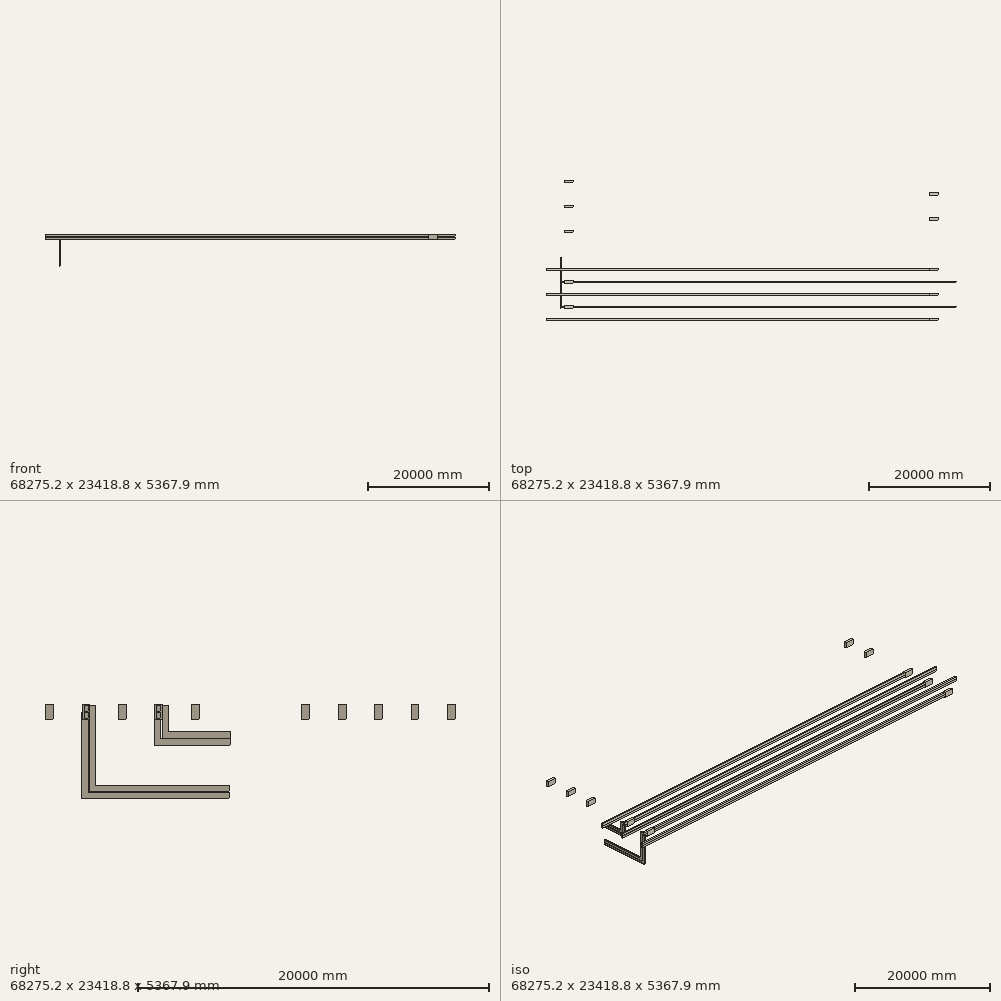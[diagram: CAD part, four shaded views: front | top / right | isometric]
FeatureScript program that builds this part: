
annotation { "Feature Type Name" : "Feature", "Feature Type Description" : "" }
export const myFeature = defineFeature(function(context is Context, id is Id, definition is map)
    precondition{}
    {
        {
            var Q0;
            Q0=qCreatedBy(makeId("Top.planeOp"),FACE);
            var sketch = newSketch(context, id + "F0", { "sketchPlane" : qUnion([Q0])});
            skLineSegment(sketch, "E0.bottom", {"start": v(-34137.6, 13411.2) * mm, "end": v(34137.6, 13411.2) * mm});
            skLineSegment(sketch, "E0.top", {"start": v(-34137.6, -13411.2) * mm, "end": v(34137.6, -13411.2) * mm});
            skLineSegment(sketch, "E0.left", {"start": v(-34137.6, 13411.2) * mm, "end": v(-34137.6, -13411.2) * mm});
            skLineSegment(sketch, "E0.right", {"start": v(34137.6, 13411.2) * mm, "end": v(34137.6, -13411.2) * mm});
            skPoint(sketch, "E0.middle", {"position": v(0, 0) * mm});
            skLineSegment(sketch, "E1", {"start": v(-31699.2, 13411.2) * mm, "end": v(-31699.2, 1219.2) * mm});
            skLineSegment(sketch, "E2", {"start": v(31699.2, 13411.2) * mm, "end": v(31699.2, 1219.2) * mm});
            skLineSegment(sketch, "E3", {"start": v(-31699.2, 1219.2) * mm, "end": v(-2438.4, 1219.2) * mm});
            skLineSegment(sketch, "E4", {"start": v(-31699.2, -1219.2) * mm, "end": v(-2438.4, -1219.2) * mm});
            skLineSegment(sketch, "E5", {"start": v(-2438.4, 13411.2) * mm, "end": v(-2438.4, 1219.2) * mm});
            skLineSegment(sketch, "E6", {"start": v(2438.4, 13411.2) * mm, "end": v(2438.4, 1219.2) * mm});
            skLineSegment(sketch, "E7.trimOffspring", {"start": v(-2438.4, -1219.2) * mm, "end": v(-2438.4, -13411.2) * mm});
            skLineSegment(sketch, "E8.trimOffspring", {"start": v(2438.4, 1219.2) * mm, "end": v(31699.2, 1219.2) * mm});
            skLineSegment(sketch, "E9.trimOffspring", {"start": v(2438.4, -1219.2) * mm, "end": v(31699.2, -1219.2) * mm});
            skLineSegment(sketch, "E10.trimOffspring", {"start": v(2438.4, -1219.2) * mm, "end": v(2438.4, -13411.2) * mm});
            skLineSegment(sketch, "E11.trimOffspring", {"start": v(-31699.2, -1219.2) * mm, "end": v(-31699.2, -13411.2) * mm});
            skLineSegment(sketch, "E12.trimOffspring", {"start": v(31699.2, -1219.2) * mm, "end": v(31699.2, -13411.2) * mm});
            skSolve(sketch);
        }
        {
            var Q0;
            {var subQ0=sQuery(id+"F0.wireOp",EDGE,"E1");Q0=makeQuery(id+"F0.imprint","IMPRINT",FACE,{"disambiguationData":[TD([[makeQuery(id+"F0.imprint","IMPRINT",EDGE,{"derivedFrom":subQ0}),1.0]])]});}
            var sketch = newSketch(context, id + "F1", { "sketchPlane" : qUnion([Q0])});
            skLineSegment(sketch, "E13.bottom", {"start": v(-31089.6, 2921) * mm, "end": v(-29616.4, 2921) * mm});
            skLineSegment(sketch, "E13.top", {"start": v(-31089.6, 3352.8) * mm, "end": v(-29616.4, 3352.8) * mm});
            skLineSegment(sketch, "E13.left", {"start": v(-31089.6, 2921) * mm, "end": v(-31089.6, 3352.8) * mm});
            skLineSegment(sketch, "E13.right", {"start": v(-29616.4, 2921) * mm, "end": v(-29616.4, 3352.8) * mm});
            skLineSegment(sketch, "E14.bottom", {"start": v(-31089.6, 7099.3) * mm, "end": v(-29616.4, 7099.3) * mm});
            skLineSegment(sketch, "E14.top", {"start": v(-31089.6, 7531.1) * mm, "end": v(-29616.4, 7531.1) * mm});
            skLineSegment(sketch, "E14.left", {"start": v(-31089.6, 7099.3) * mm, "end": v(-31089.6, 7531.1) * mm});
            skLineSegment(sketch, "E14.right", {"start": v(-29616.4, 7099.3) * mm, "end": v(-29616.4, 7531.1) * mm});
            skLineSegment(sketch, "E15.bottom", {"start": v(-31089.6, 11277.6) * mm, "end": v(-29616.4, 11277.6) * mm});
            skLineSegment(sketch, "E15.top", {"start": v(-31089.6, 11709.4) * mm, "end": v(-29616.4, 11709.4) * mm});
            skLineSegment(sketch, "E15.left", {"start": v(-31089.6, 11277.6) * mm, "end": v(-31089.6, 11709.4) * mm});
            skLineSegment(sketch, "E15.right", {"start": v(-29616.4, 11277.6) * mm, "end": v(-29616.4, 11709.4) * mm});
            skLineSegment(sketch, "E16.bottom", {"start": v(-31089.6, -9169.4) * mm, "end": v(-29616.4, -9169.4) * mm});
            skLineSegment(sketch, "E16.top", {"start": v(-31089.6, -9601.2) * mm, "end": v(-29616.4, -9601.2) * mm});
            skLineSegment(sketch, "E16.left", {"start": v(-31089.6, -9169.4) * mm, "end": v(-31089.6, -9601.2) * mm});
            skLineSegment(sketch, "E16.right", {"start": v(-29616.4, -9169.4) * mm, "end": v(-29616.4, -9601.2) * mm});
            skPoint(sketch, "E17.left.start.orphan", {"position": v(-31089.6, -5029.2) * mm});
            skLineSegment(sketch, "E18.bottom", {"start": v(-31089.6, -5029.2) * mm, "end": v(-29616.4, -5029.2) * mm});
            skLineSegment(sketch, "E18.top", {"start": v(-31089.6, -5461) * mm, "end": v(-29616.4, -5461) * mm});
            skLineSegment(sketch, "E18.left", {"start": v(-31089.6, -5029.2) * mm, "end": v(-31089.6, -5461) * mm});
            skLineSegment(sketch, "E18.right", {"start": v(-29616.4, -5029.2) * mm, "end": v(-29616.4, -5461) * mm});
            skLineSegment(sketch, "E19.bottom", {"start": v(31089.6, -7531.1) * mm, "end": v(29616.4, -7531.1) * mm});
            skLineSegment(sketch, "E19.top", {"start": v(31089.6, -7099.3) * mm, "end": v(29616.4, -7099.3) * mm});
            skLineSegment(sketch, "E19.left", {"start": v(31089.6, -7531.1) * mm, "end": v(31089.6, -7099.3) * mm});
            skLineSegment(sketch, "E19.right", {"start": v(29616.4, -7531.1) * mm, "end": v(29616.4, -7099.3) * mm});
            skLineSegment(sketch, "E20.bottom", {"start": v(31089.6, -11709.4) * mm, "end": v(29616.4, -11709.4) * mm});
            skLineSegment(sketch, "E20.top", {"start": v(31089.6, -11277.6) * mm, "end": v(29616.4, -11277.6) * mm});
            skLineSegment(sketch, "E20.left", {"start": v(31089.6, -11709.4) * mm, "end": v(31089.6, -11277.6) * mm});
            skLineSegment(sketch, "E20.right", {"start": v(29616.4, -11709.4) * mm, "end": v(29616.4, -11277.6) * mm});
            skLineSegment(sketch, "E21.bottom", {"start": v(31089.6, -3352.8) * mm, "end": v(29616.4, -3352.8) * mm});
            skLineSegment(sketch, "E21.top", {"start": v(31089.6, -2921) * mm, "end": v(29616.4, -2921) * mm});
            skLineSegment(sketch, "E21.left", {"start": v(31089.6, -3352.8) * mm, "end": v(31089.6, -2921) * mm});
            skLineSegment(sketch, "E21.right", {"start": v(29616.4, -3352.8) * mm, "end": v(29616.4, -2921) * mm});
            skPoint(sketch, "E22.oppositeSnap0", {"position": v(29616.4, -3136.9) * mm});
            skLineSegment(sketch, "E22.bottom", {"start": v(31089.6, 5029.2) * mm, "end": v(29616.4, 5029.2) * mm});
            skLineSegment(sketch, "E22.top", {"start": v(31089.6, 5461) * mm, "end": v(29616.4, 5461) * mm});
            skLineSegment(sketch, "E22.left", {"start": v(31089.6, 5029.2) * mm, "end": v(31089.6, 5461) * mm});
            skLineSegment(sketch, "E22.right", {"start": v(29616.4, 5029.2) * mm, "end": v(29616.4, 5461) * mm});
            skLineSegment(sketch, "E23.bottom", {"start": v(31089.6, 9169.4) * mm, "end": v(29616.4, 9169.4) * mm});
            skLineSegment(sketch, "E23.top", {"start": v(31089.6, 9601.2) * mm, "end": v(29616.4, 9601.2) * mm});
            skLineSegment(sketch, "E23.left", {"start": v(31089.6, 9169.4) * mm, "end": v(31089.6, 9601.2) * mm});
            skLineSegment(sketch, "E23.right", {"start": v(29616.4, 9169.4) * mm, "end": v(29616.4, 9601.2) * mm});
            skSolve(sketch);
        }
        {
            var Q0;
            Q0=qSketchRegion(id+"F1",true);
            extrude(context, id + "F2", {"entities" : qUnion([Q0]), "depth" : 838.2 * mm, "offsetDistance" : 25.4 * mm});
        }
        {
            var Q0;
            Q0=makeQuery(id+"F2.opExtrude","SWEPT_FACE",FACE,{"disambiguationData":[OSD([sQuery(id+"F1.wireOp",EDGE,"E16.right")])]});
            var sketch = newSketch(context, id + "F3", { "sketchPlane" : qUnion([Q0])});
            skLineSegment(sketch, "E24.bottom", {"start": v(-9271, 42.33) * mm, "end": v(-9499.6, 42.33) * mm});
            skLineSegment(sketch, "E24.top", {"start": v(-9271, 397.93) * mm, "end": v(-9499.6, 397.93) * mm});
            skLineSegment(sketch, "E24.left", {"start": v(-9271, 42.33) * mm, "end": v(-9271, 397.93) * mm});
            skLineSegment(sketch, "E24.right", {"start": v(-9499.6, 42.33) * mm, "end": v(-9499.6, 397.93) * mm});
            skPoint(sketch, "E24.middle", {"position": v(-9385.3, 220.13) * mm});
            skPoint(sketch, "E24.middle.positionSnap0", {"position": v(-9385.3, 0) * mm});
            skPoint(sketch, "E24.centerSnap0", {"position": v(-9385.3, 0) * mm});
            skLineSegment(sketch, "E25.bottom", {"start": v(-9499.6, 440.27) * mm, "end": v(-9271, 440.27) * mm});
            skLineSegment(sketch, "E25.top", {"start": v(-9499.6, 795.87) * mm, "end": v(-9271, 795.87) * mm});
            skLineSegment(sketch, "E25.left", {"start": v(-9499.6, 440.27) * mm, "end": v(-9499.6, 795.87) * mm});
            skLineSegment(sketch, "E25.right", {"start": v(-9271, 440.27) * mm, "end": v(-9271, 795.87) * mm});
            skPoint(sketch, "E25.middle", {"position": v(-9385.3, 618.07) * mm});
            skLineSegment(sketch, "E26.bottom", {"start": v(-5359.4, 397.93) * mm, "end": v(-5130.8, 397.93) * mm});
            skLineSegment(sketch, "E26.top", {"start": v(-5359.4, 42.33) * mm, "end": v(-5130.8, 42.33) * mm});
            skLineSegment(sketch, "E26.left", {"start": v(-5359.4, 397.93) * mm, "end": v(-5359.4, 42.33) * mm});
            skLineSegment(sketch, "E26.right", {"start": v(-5130.8, 397.93) * mm, "end": v(-5130.8, 42.33) * mm});
            skPoint(sketch, "E26.middle", {"position": v(-5245.1, 220.13) * mm});
            skLineSegment(sketch, "E27.bottom", {"start": v(-5359.4, 440.27) * mm, "end": v(-5130.8, 440.27) * mm});
            skLineSegment(sketch, "E27.top", {"start": v(-5359.4, 795.87) * mm, "end": v(-5130.8, 795.87) * mm});
            skLineSegment(sketch, "E27.left", {"start": v(-5359.4, 440.27) * mm, "end": v(-5359.4, 795.87) * mm});
            skLineSegment(sketch, "E27.right", {"start": v(-5130.8, 440.27) * mm, "end": v(-5130.8, 795.87) * mm});
            skPoint(sketch, "E27.middle", {"position": v(-5245.1, 618.07) * mm});
            skSolve(sketch);
        }
        {
            var Q0;
            Q0=qSketchRegion(id+"F3",true);
            extrude(context, id + "F4", {"entities" : qUnion([Q0]), "depth" : 63754 * mm, "offsetDistance" : 25.4 * mm});
        }
        {
            var Q0;
            Q0=makeQuery(id+"F2.opExtrude","SWEPT_FACE",FACE,{"disambiguationData":[OSD([sQuery(id+"F1.wireOp",EDGE,"E21.right")])]});
            var sketch = newSketch(context, id + "F5", { "sketchPlane" : qUnion([Q0])});
            skLineSegment(sketch, "E28.bottom", {"start": v(3022.6, 397.93) * mm, "end": v(3251.2, 397.93) * mm});
            skLineSegment(sketch, "E28.top", {"start": v(3022.6, 42.33) * mm, "end": v(3251.2, 42.33) * mm});
            skLineSegment(sketch, "E28.left", {"start": v(3022.6, 397.93) * mm, "end": v(3022.6, 42.33) * mm});
            skLineSegment(sketch, "E28.right", {"start": v(3251.2, 397.93) * mm, "end": v(3251.2, 42.33) * mm});
            skPoint(sketch, "E28.middle", {"position": v(3136.9, 220.13) * mm});
            skPoint(sketch, "E28.middle.positionSnap0", {"position": v(3136.9, 0) * mm});
            skPoint(sketch, "E28.centerSnap0", {"position": v(3136.9, 0) * mm});
            skLineSegment(sketch, "E29.bottom", {"start": v(3022.6, 440.27) * mm, "end": v(3251.2, 440.27) * mm});
            skLineSegment(sketch, "E29.top", {"start": v(3022.6, 795.87) * mm, "end": v(3251.2, 795.87) * mm});
            skLineSegment(sketch, "E29.left", {"start": v(3022.6, 440.27) * mm, "end": v(3022.6, 795.87) * mm});
            skLineSegment(sketch, "E29.right", {"start": v(3251.2, 440.27) * mm, "end": v(3251.2, 795.87) * mm});
            skPoint(sketch, "E29.middle", {"position": v(3136.9, 618.07) * mm});
            skLineSegment(sketch, "E30.bottom", {"start": v(7200.9, 397.93) * mm, "end": v(7429.5, 397.93) * mm});
            skLineSegment(sketch, "E30.top", {"start": v(7200.9, 42.33) * mm, "end": v(7429.5, 42.33) * mm});
            skLineSegment(sketch, "E30.left", {"start": v(7200.9, 397.93) * mm, "end": v(7200.9, 42.33) * mm});
            skLineSegment(sketch, "E30.right", {"start": v(7429.5, 397.93) * mm, "end": v(7429.5, 42.33) * mm});
            skPoint(sketch, "E30.middle", {"position": v(7315.2, 220.13) * mm});
            skLineSegment(sketch, "E31.bottom", {"start": v(7200.9, 795.87) * mm, "end": v(7429.5, 795.87) * mm});
            skLineSegment(sketch, "E31.top", {"start": v(7200.9, 440.27) * mm, "end": v(7429.5, 440.27) * mm});
            skLineSegment(sketch, "E31.left", {"start": v(7200.9, 795.87) * mm, "end": v(7200.9, 440.27) * mm});
            skLineSegment(sketch, "E31.right", {"start": v(7429.5, 795.87) * mm, "end": v(7429.5, 440.27) * mm});
            skPoint(sketch, "E31.middle", {"position": v(7315.2, 618.07) * mm});
            skLineSegment(sketch, "E32.bottom", {"start": v(11379.2, 397.93) * mm, "end": v(11607.8, 397.93) * mm});
            skLineSegment(sketch, "E32.top", {"start": v(11379.2, 42.33) * mm, "end": v(11607.8, 42.33) * mm});
            skLineSegment(sketch, "E32.left", {"start": v(11379.2, 397.93) * mm, "end": v(11379.2, 42.33) * mm});
            skLineSegment(sketch, "E32.right", {"start": v(11607.8, 397.93) * mm, "end": v(11607.8, 42.33) * mm});
            skPoint(sketch, "E32.middle", {"position": v(11493.5, 220.13) * mm});
            skLineSegment(sketch, "E33.bottom", {"start": v(11379.2, 440.27) * mm, "end": v(11607.8, 440.27) * mm});
            skLineSegment(sketch, "E33.top", {"start": v(11379.2, 795.87) * mm, "end": v(11607.8, 795.87) * mm});
            skLineSegment(sketch, "E33.left", {"start": v(11379.2, 440.27) * mm, "end": v(11379.2, 795.87) * mm});
            skLineSegment(sketch, "E33.right", {"start": v(11607.8, 440.27) * mm, "end": v(11607.8, 795.87) * mm});
            skPoint(sketch, "E33.middle", {"position": v(11493.5, 618.07) * mm});
            skSolve(sketch);
        }
        {
            var Q0;
            Q0=qSketchRegion(id+"F5",true);
            extrude(context, id + "F6", {"entities" : qUnion([Q0]), "depth" : 63754 * mm, "offsetDistance" : 25.4 * mm});
        }
        {
            var Q0;
            Q0=makeQuery(id+"F2.opExtrude","SWEPT_FACE",FACE,{"disambiguationData":[OSD([sQuery(id+"F1.wireOp",EDGE,"E18.left")])]});
            var sketch = newSketch(context, id + "F7", { "sketchPlane" : qUnion([Q0])});
            skLineSegment(sketch, "E34.bottom", {"start": v(5130.8, 397.93) * mm, "end": v(5359.4, 397.93) * mm});
            skLineSegment(sketch, "E34.top", {"start": v(5130.8, 42.33) * mm, "end": v(5359.4, 42.33) * mm});
            skLineSegment(sketch, "E34.left", {"start": v(5130.8, 397.93) * mm, "end": v(5130.8, 42.33) * mm});
            skLineSegment(sketch, "E34.right", {"start": v(5359.4, 397.93) * mm, "end": v(5359.4, 42.33) * mm});
            skPoint(sketch, "E34.middle", {"position": v(5245.1, 220.13) * mm});
            skPoint(sketch, "E34.middle.positionSnap0", {"position": v(5245.1, 0) * mm});
            skPoint(sketch, "E34.centerSnap0", {"position": v(5245.1, 0) * mm});
            skLineSegment(sketch, "E35.bottom", {"start": v(5130.8, 440.27) * mm, "end": v(5359.4, 440.27) * mm});
            skLineSegment(sketch, "E35.top", {"start": v(5130.8, 795.87) * mm, "end": v(5359.4, 795.87) * mm});
            skLineSegment(sketch, "E35.left", {"start": v(5130.8, 440.27) * mm, "end": v(5130.8, 795.87) * mm});
            skLineSegment(sketch, "E35.right", {"start": v(5359.4, 440.27) * mm, "end": v(5359.4, 795.87) * mm});
            skPoint(sketch, "E35.middle", {"position": v(5245.1, 618.07) * mm});
            skLineSegment(sketch, "E36.bottom", {"start": v(9271, 42.33) * mm, "end": v(9499.6, 42.33) * mm});
            skLineSegment(sketch, "E36.top", {"start": v(9271, 397.93) * mm, "end": v(9499.6, 397.93) * mm});
            skLineSegment(sketch, "E36.left", {"start": v(9271, 42.33) * mm, "end": v(9271, 397.93) * mm});
            skLineSegment(sketch, "E36.right", {"start": v(9499.6, 42.33) * mm, "end": v(9499.6, 397.93) * mm});
            skPoint(sketch, "E36.middle", {"position": v(9385.3, 220.13) * mm});
            skLineSegment(sketch, "E37.bottom", {"start": v(9271, 440.27) * mm, "end": v(9499.6, 440.27) * mm});
            skLineSegment(sketch, "E37.top", {"start": v(9271, 795.87) * mm, "end": v(9499.6, 795.87) * mm});
            skLineSegment(sketch, "E37.left", {"start": v(9271, 440.27) * mm, "end": v(9271, 795.87) * mm});
            skLineSegment(sketch, "E37.right", {"start": v(9499.6, 440.27) * mm, "end": v(9499.6, 795.87) * mm});
            skPoint(sketch, "E37.middle", {"position": v(9385.3, 618.07) * mm});
            skSolve(sketch);
        }
        {
            var Q0;
            Q0 = qSketchRegion(id + "F7", true);
            extrude(context, id + "F8", {"entities" : qUnion([Q0]), "depth" : 723.9 * mm, "offsetDistance" : 25.4 * mm});
        }
        {
            var Q0;
            Q0=makeQuery(id+"F8.opExtrude","SWEPT_FACE",FACE,{"disambiguationData":[OSD([sQuery(id+"F7.wireOp",EDGE,"E35.left")])]});
            var sketch = newSketch(context, id + "F9", { "sketchPlane" : qUnion([Q0])});
            skLineSegment(sketch, "E38.bottom", {"start": v(31813.5, 795.87) * mm, "end": v(31584.9, 795.87) * mm});
            skLineSegment(sketch, "E38.top", {"start": v(31813.5, 440.27) * mm, "end": v(31584.9, 440.27) * mm});
            skLineSegment(sketch, "E38.left", {"start": v(31813.5, 795.87) * mm, "end": v(31813.5, 440.27) * mm});
            skLineSegment(sketch, "E38.right", {"start": v(31584.9, 795.87) * mm, "end": v(31584.9, 440.27) * mm});
            skSolve(sketch);
        }
        {
            var Q0;
            Q0 = qSketchRegion(id + "F9", true);
            extrude(context, id + "F10", {"entities" : qUnion([Q0]), "operationType" : NewBodyOperationType.ADD, "depth" : 431.8 * mm, "offsetDistance" : 25.4 * mm});
        }
        {
            var Q0;
            Q0=makeQuery(id+"F8.opExtrude","SWEPT_FACE",FACE,{"disambiguationData":[OSD([sQuery(id+"F7.wireOp",EDGE,"E34.right")])]});
            var sketch = newSketch(context, id + "F11", { "sketchPlane" : qUnion([Q0])});
            skLineSegment(sketch, "E39.bottom", {"start": v(-31813.5, 42.33) * mm, "end": v(-31584.9, 42.33) * mm});
            skLineSegment(sketch, "E39.top", {"start": v(-31813.5, 397.93) * mm, "end": v(-31584.9, 397.93) * mm});
            skLineSegment(sketch, "E39.left", {"start": v(-31813.5, 42.33) * mm, "end": v(-31813.5, 397.93) * mm});
            skLineSegment(sketch, "E39.right", {"start": v(-31584.9, 42.33) * mm, "end": v(-31584.9, 397.93) * mm});
            skSolve(sketch);
        }
        {
            var Q0;
            Q0 = qSketchRegion(id + "F11", true);
            extrude(context, id + "F12", {"entities" : qUnion([Q0]), "operationType" : NewBodyOperationType.ADD, "depth" : 127 * mm, "offsetDistance" : 25.4 * mm});
        }
        {
            var Q0;
            Q0=makeQuery(id+"F12.boolean.opBoolean","MERGE",FACE,{"derivedFrom":[makeQuery(id+"F8.opExtrude","SWEPT_FACE",FACE,{"disambiguationData":[OSD([sQuery(id+"F7.wireOp",EDGE,"E34.top")])]}),makeQuery(id+"F12.opExtrude","SWEPT_FACE",FACE,{"disambiguationData":[OSD([sQuery(id+"F11.wireOp",EDGE,"E39.bottom")])]})]});
            var sketch = newSketch(context, id + "F13", { "sketchPlane" : qUnion([Q0])});
            skLineSegment(sketch, "E40.bottom", {"start": v(-31813.5, 5486.4) * mm, "end": v(-31584.9, 5486.4) * mm});
            skLineSegment(sketch, "E40.top", {"start": v(-31813.5, 5130.8) * mm, "end": v(-31584.9, 5130.8) * mm});
            skLineSegment(sketch, "E40.left", {"start": v(-31813.5, 5486.4) * mm, "end": v(-31813.5, 5130.8) * mm});
            skLineSegment(sketch, "E40.right", {"start": v(-31584.9, 5486.4) * mm, "end": v(-31584.9, 5130.8) * mm});
            skSolve(sketch);
        }
        {
            var Q0;
            Q0 = qSketchRegion(id + "F13", true);
            extrude(context, id + "F14", {"entities" : qUnion([Q0]), "operationType" : NewBodyOperationType.ADD, "depth" : 1524 * mm, "offsetDistance" : 25.4 * mm});
        }
        {
            var Q0;
            Q0=makeQuery(id+"F10.boolean.opBoolean","MERGE",FACE,{"derivedFrom":[makeQuery(id+"F8.opExtrude","SWEPT_FACE",FACE,{"disambiguationData":[OSD([sQuery(id+"F7.wireOp",EDGE,"E35.bottom")])]}),makeQuery(id+"F10.opExtrude","SWEPT_FACE",FACE,{"disambiguationData":[OSD([sQuery(id+"F9.wireOp",EDGE,"E38.top")])]})]});
            var sketch = newSketch(context, id + "F15", { "sketchPlane" : qUnion([Q0])});
            skLineSegment(sketch, "E41.bottom", {"start": v(-31584.9, 4699) * mm, "end": v(-31813.5, 4699) * mm});
            skLineSegment(sketch, "E41.top", {"start": v(-31584.9, 5054.6) * mm, "end": v(-31813.5, 5054.6) * mm});
            skLineSegment(sketch, "E41.left", {"start": v(-31584.9, 4699) * mm, "end": v(-31584.9, 5054.6) * mm});
            skLineSegment(sketch, "E41.right", {"start": v(-31813.5, 4699) * mm, "end": v(-31813.5, 5054.6) * mm});
            skSolve(sketch);
        }
        {
            var Q0;
            Q0 = qSketchRegion(id + "F15", true);
            extrude(context, id + "F16", {"entities" : qUnion([Q0]), "operationType" : NewBodyOperationType.ADD, "depth" : 1524 * mm, "offsetDistance" : 25.4 * mm});
        }
        {
            var Q0;
            Q0=makeQuery(id+"F16.boolean.opBoolean","MERGE",FACE,{"derivedFrom":[makeQuery(id+"F10.opExtrude","CAP_FACE",FACE,{"disambiguationData":[OSD([sQuery(id+"F9.wireOp",EDGE,"E38.bottom"),sQuery(id+"F9.wireOp",EDGE,"E38.top"),sQuery(id+"F9.wireOp",EDGE,"E38.left"),sQuery(id+"F9.wireOp",EDGE,"E38.right")])],"isStart":false}),makeQuery(id+"F16.opExtrude","SWEPT_FACE",FACE,{"disambiguationData":[OSD([sQuery(id+"F15.wireOp",EDGE,"E41.bottom")])]})]});
            var sketch = newSketch(context, id + "F17", { "sketchPlane" : qUnion([Q0])});
            skLineSegment(sketch, "E42.bottom", {"start": v(31584.9, -1083.73) * mm, "end": v(31813.5, -1083.73) * mm});
            skLineSegment(sketch, "E42.top", {"start": v(31584.9, -728.13) * mm, "end": v(31813.5, -728.13) * mm});
            skLineSegment(sketch, "E42.left", {"start": v(31584.9, -1083.73) * mm, "end": v(31584.9, -728.13) * mm});
            skLineSegment(sketch, "E42.right", {"start": v(31813.5, -1083.73) * mm, "end": v(31813.5, -728.13) * mm});
            skSolve(sketch);
        }
        {
            var Q0;
            Q0=makeQuery(id+"F14.boolean.opBoolean","MERGE",FACE,{"derivedFrom":[makeQuery(id+"F8.opExtrude","SWEPT_FACE",FACE,{"disambiguationData":[OSD([sQuery(id+"F7.wireOp",EDGE,"E34.left")])]}),makeQuery(id+"F14.opExtrude","SWEPT_FACE",FACE,{"disambiguationData":[OSD([sQuery(id+"F13.wireOp",EDGE,"E40.top")])]})]});
            var sketch = newSketch(context, id + "F18", { "sketchPlane" : qUnion([Q0])});
            skLineSegment(sketch, "E43.bottom", {"start": v(31584.9, -1481.67) * mm, "end": v(31813.5, -1481.67) * mm});
            skLineSegment(sketch, "E43.top", {"start": v(31584.9, -1126.07) * mm, "end": v(31813.5, -1126.07) * mm});
            skLineSegment(sketch, "E43.left", {"start": v(31584.9, -1481.67) * mm, "end": v(31584.9, -1126.07) * mm});
            skLineSegment(sketch, "E43.right", {"start": v(31813.5, -1481.67) * mm, "end": v(31813.5, -1126.07) * mm});
            skSolve(sketch);
        }
        {
            var Q0;
            Q0 = qSketchRegion(id + "F17", true);
            extrude(context, id + "F19", {"entities" : qUnion([Q0]), "operationType" : NewBodyOperationType.ADD, "depth" : 3556 * mm, "offsetDistance" : 25.4 * mm});
        }
        {
            var Q0;
            Q0 = qSketchRegion(id + "F17", true);
            extrude(context, id + "F20", {"entities" : qUnion([Q0]), "operationType" : NewBodyOperationType.ADD, "depth" : 3556 * mm, "offsetDistance" : 25.4 * mm});
        }
        {
            var Q0;
            Q0 = qSketchRegion(id + "F18", true);
            extrude(context, id + "F21", {"entities" : qUnion([Q0]), "operationType" : NewBodyOperationType.ADD, "depth" : 3987.8 * mm, "offsetDistance" : 25.4 * mm});
        }
        {
            var Q0;
            Q0=makeQuery(id+"F8.opExtrude","SWEPT_FACE",FACE,{"disambiguationData":[OSD([sQuery(id+"F7.wireOp",EDGE,"E37.left")])]});
            var sketch = newSketch(context, id + "F22", { "sketchPlane" : qUnion([Q0])});
            skLineSegment(sketch, "E44.bottom", {"start": v(31813.5, 795.87) * mm, "end": v(31584.9, 795.87) * mm});
            skLineSegment(sketch, "E44.top", {"start": v(31813.5, 440.27) * mm, "end": v(31584.9, 440.27) * mm});
            skLineSegment(sketch, "E44.left", {"start": v(31813.5, 795.87) * mm, "end": v(31813.5, 440.27) * mm});
            skLineSegment(sketch, "E44.right", {"start": v(31584.9, 795.87) * mm, "end": v(31584.9, 440.27) * mm});
            skSolve(sketch);
        }
        {
            var Q0;
            Q0 = qSketchRegion(id + "F22", true);
            extrude(context, id + "F23", {"entities" : qUnion([Q0]), "operationType" : NewBodyOperationType.ADD, "depth" : 431.8 * mm, "offsetDistance" : 25.4 * mm});
        }
        {
            var Q0;
            Q0=makeQuery(id+"F8.opExtrude","SWEPT_FACE",FACE,{"disambiguationData":[OSD([sQuery(id+"F7.wireOp",EDGE,"E36.right")])]});
            var sketch = newSketch(context, id + "F24", { "sketchPlane" : qUnion([Q0])});
            skLineSegment(sketch, "E45.bottom", {"start": v(-31813.5, 42.33) * mm, "end": v(-31584.9, 42.33) * mm});
            skLineSegment(sketch, "E45.top", {"start": v(-31813.5, 397.93) * mm, "end": v(-31584.9, 397.93) * mm});
            skLineSegment(sketch, "E45.left", {"start": v(-31813.5, 42.33) * mm, "end": v(-31813.5, 397.93) * mm});
            skLineSegment(sketch, "E45.right", {"start": v(-31584.9, 42.33) * mm, "end": v(-31584.9, 397.93) * mm});
            skSolve(sketch);
        }
        {
            var Q0;
            Q0 = qSketchRegion(id + "F24", true);
            extrude(context, id + "F25", {"entities" : qUnion([Q0]), "operationType" : NewBodyOperationType.ADD, "depth" : 127 * mm, "offsetDistance" : 25.4 * mm});
        }
        {
            var Q0;
            Q0=makeQuery(id+"F25.boolean.opBoolean","MERGE",FACE,{"derivedFrom":[makeQuery(id+"F8.opExtrude","SWEPT_FACE",FACE,{"disambiguationData":[OSD([sQuery(id+"F7.wireOp",EDGE,"E36.bottom")])]}),makeQuery(id+"F25.opExtrude","SWEPT_FACE",FACE,{"disambiguationData":[OSD([sQuery(id+"F24.wireOp",EDGE,"E45.bottom")])]})]});
            var sketch = newSketch(context, id + "F26", { "sketchPlane" : qUnion([Q0])});
            skLineSegment(sketch, "E46.bottom", {"start": v(-31813.5, 9626.6) * mm, "end": v(-31584.9, 9626.6) * mm});
            skLineSegment(sketch, "E46.top", {"start": v(-31813.5, 9271) * mm, "end": v(-31584.9, 9271) * mm});
            skLineSegment(sketch, "E46.left", {"start": v(-31813.5, 9626.6) * mm, "end": v(-31813.5, 9271) * mm});
            skLineSegment(sketch, "E46.right", {"start": v(-31584.9, 9626.6) * mm, "end": v(-31584.9, 9271) * mm});
            skSolve(sketch);
        }
        {
            var Q0;
            {var subQ4=sQuery(id+"F26.wireOp",EDGE,"E46.bottom");Q0=makeQuery(id+"F26.imprint","IMPRINT",FACE,{"disambiguationData":[TD([[makeQuery(id+"F26.imprint","IMPRINT",EDGE,{"derivedFrom":subQ4}),-1.0]])]});}
            extrude(context, id + "F27", {"entities" : qUnion([Q0]), "operationType" : NewBodyOperationType.ADD, "depth" : 4572 * mm, "offsetDistance" : 25.4 * mm});
        }
        {
            var Q0;
            Q0=makeQuery(id+"F23.boolean.opBoolean","MERGE",FACE,{"derivedFrom":[makeQuery(id+"F8.opExtrude","SWEPT_FACE",FACE,{"disambiguationData":[OSD([sQuery(id+"F7.wireOp",EDGE,"E37.bottom")])]}),makeQuery(id+"F23.opExtrude","SWEPT_FACE",FACE,{"disambiguationData":[OSD([sQuery(id+"F22.wireOp",EDGE,"E44.top")])]})]});
            var sketch = newSketch(context, id + "F28", { "sketchPlane" : qUnion([Q0])});
            skLineSegment(sketch, "E47.bottom", {"start": v(-31813.5, 8839.2) * mm, "end": v(-31584.9, 8839.2) * mm});
            skLineSegment(sketch, "E47.top", {"start": v(-31813.5, 9194.8) * mm, "end": v(-31584.9, 9194.8) * mm});
            skLineSegment(sketch, "E47.left", {"start": v(-31813.5, 8839.2) * mm, "end": v(-31813.5, 9194.8) * mm});
            skLineSegment(sketch, "E47.right", {"start": v(-31584.9, 8839.2) * mm, "end": v(-31584.9, 9194.8) * mm});
            skSolve(sketch);
        }
        {
            var Q0;
            Q0 = qSketchRegion(id + "F28", true);
            extrude(context, id + "F29", {"entities" : qUnion([Q0]), "operationType" : NewBodyOperationType.ADD, "depth" : 4572 * mm, "offsetDistance" : 25.4 * mm});
        }
        {
            var Q0;
            Q0=makeQuery(id+"F29.boolean.opBoolean","MERGE",FACE,{"derivedFrom":[makeQuery(id+"F23.opExtrude","CAP_FACE",FACE,{"disambiguationData":[OSD([sQuery(id+"F22.wireOp",EDGE,"E44.bottom"),sQuery(id+"F22.wireOp",EDGE,"E44.top"),sQuery(id+"F22.wireOp",EDGE,"E44.left"),sQuery(id+"F22.wireOp",EDGE,"E44.right")])],"isStart":false}),makeQuery(id+"F29.opExtrude","SWEPT_FACE",FACE,{"disambiguationData":[OSD([sQuery(id+"F28.wireOp",EDGE,"E47.bottom")])]})]});
            var sketch = newSketch(context, id + "F30", { "sketchPlane" : qUnion([Q0])});
            skLineSegment(sketch, "E48.bottom", {"start": v(31584.9, -4131.73) * mm, "end": v(31813.5, -4131.73) * mm});
            skLineSegment(sketch, "E48.top", {"start": v(31584.9, -3776.13) * mm, "end": v(31813.5, -3776.13) * mm});
            skLineSegment(sketch, "E48.left", {"start": v(31584.9, -4131.73) * mm, "end": v(31584.9, -3776.13) * mm});
            skLineSegment(sketch, "E48.right", {"start": v(31813.5, -4131.73) * mm, "end": v(31813.5, -3776.13) * mm});
            skSolve(sketch);
        }
        {
            var Q0;
            Q0=makeQuery(id+"F30.imprint","IMPRINT",FACE,{"disambiguationData":[TD([[makeQuery(id+"F30.imprint","IMPRINT",EDGE,{"derivedFrom":sQuery(id+"F30.wireOp",EDGE,"E48.bottom")}),-1.0]])]});
            extrude(context, id + "F31", {"entities" : qUnion([Q0]), "operationType" : NewBodyOperationType.ADD, "depth" : 7620 * mm, "offsetDistance" : 25.4 * mm});
        }
        {
            var Q0;
            Q0=makeQuery(id+"F27.boolean.opBoolean","MERGE",FACE,{"derivedFrom":[makeQuery(id+"F8.opExtrude","SWEPT_FACE",FACE,{"disambiguationData":[OSD([sQuery(id+"F7.wireOp",EDGE,"E36.left")])]}),makeQuery(id+"F27.opExtrude","SWEPT_FACE",FACE,{"disambiguationData":[OSD([sQuery(id+"F26.wireOp",EDGE,"E46.top")])]})]});
            var sketch = newSketch(context, id + "F32", { "sketchPlane" : qUnion([Q0])});
            skLineSegment(sketch, "E49.bottom", {"start": v(31813.5, -4529.67) * mm, "end": v(31584.9, -4529.67) * mm});
            skLineSegment(sketch, "E49.top", {"start": v(31813.5, -4174.07) * mm, "end": v(31584.9, -4174.07) * mm});
            skLineSegment(sketch, "E49.left", {"start": v(31813.5, -4529.67) * mm, "end": v(31813.5, -4174.07) * mm});
            skLineSegment(sketch, "E49.right", {"start": v(31584.9, -4529.67) * mm, "end": v(31584.9, -4174.07) * mm});
            skSolve(sketch);
        }
        {
            var Q0;
            Q0 = qSketchRegion(id + "F32", true);
            extrude(context, id + "F33", {"entities" : qUnion([Q0]), "operationType" : NewBodyOperationType.ADD, "depth" : 8051.8 * mm, "offsetDistance" : 25.4 * mm});
        }
    });
